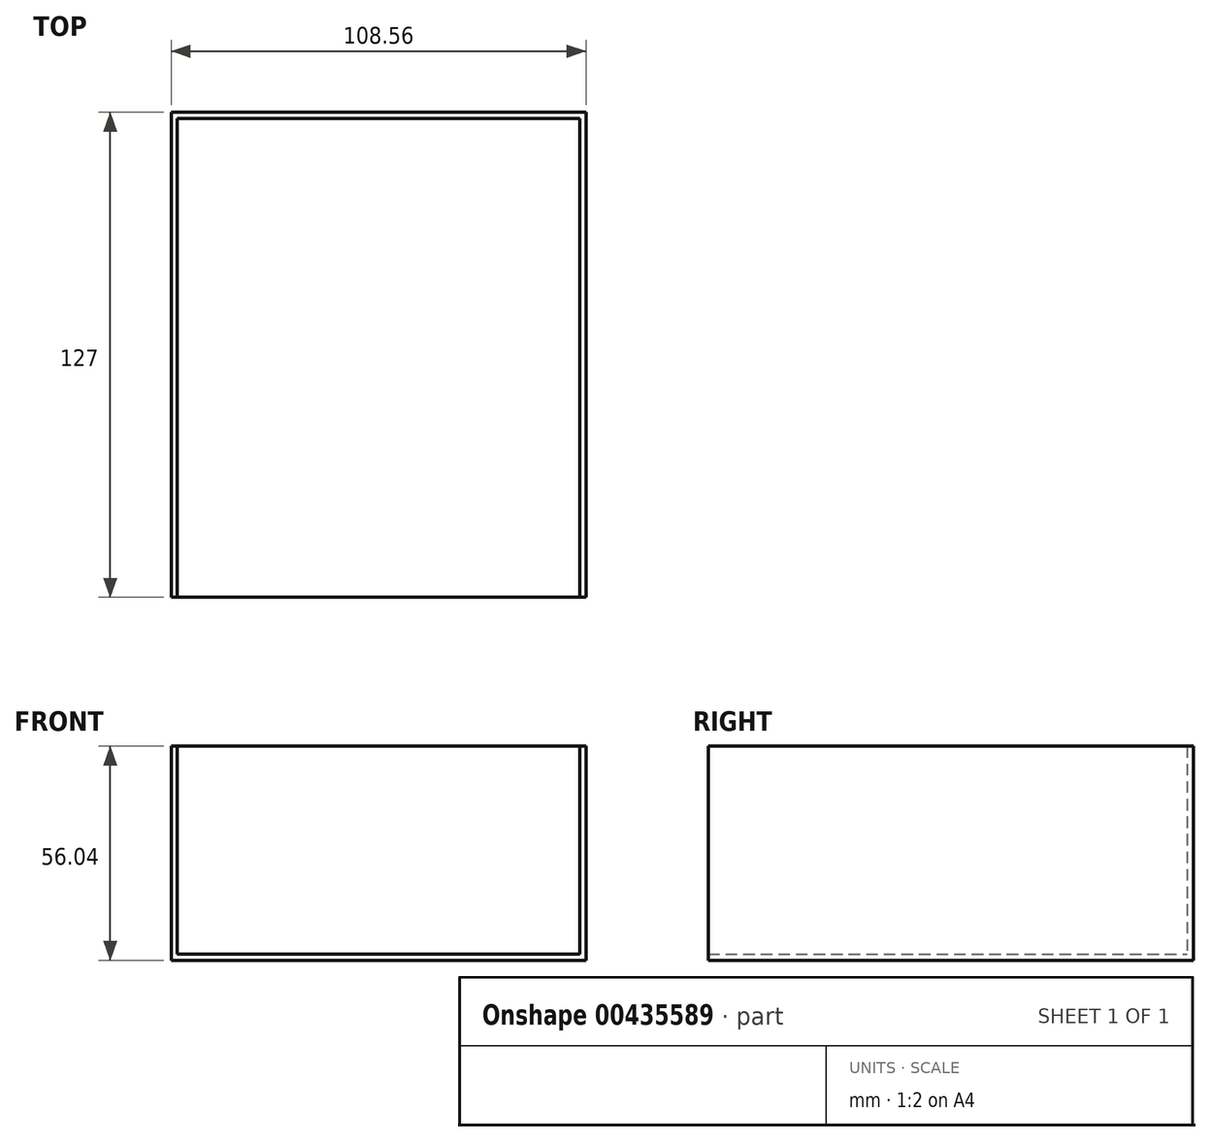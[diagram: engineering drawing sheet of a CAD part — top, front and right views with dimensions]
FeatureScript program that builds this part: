
annotation { "Feature Type Name" : "Feature", "Feature Type Description" : "" }
export const myFeature = defineFeature(function(context is Context, id is Id, definition is map)
    precondition{}
    {
        {
            var Q0;
            Q0=qCreatedBy(makeId("Front.planeOp"),FACE);
            var sketch = newSketch(context, id + "F0", { "sketchPlane" : qUnion([Q0])});
            skLineSegment(sketch, "E0.bottom", {"start": v(-54.28, 28.02) * mm, "end": v(54.28, 28.02) * mm});
            skLineSegment(sketch, "E0.top", {"start": v(-54.28, -28.02) * mm, "end": v(54.28, -28.02) * mm});
            skLineSegment(sketch, "E0.left", {"start": v(-54.28, 28.02) * mm, "end": v(-54.28, -28.02) * mm});
            skLineSegment(sketch, "E0.right", {"start": v(54.28, 28.02) * mm, "end": v(54.28, -28.02) * mm});
            skPoint(sketch, "E0.middle", {"position": v(0, 0) * mm});
            skSolve(sketch);
        }
        {
            var Q0;
            Q0 = qSketchRegion(id + "F0", true);
            extrude(context, id + "F1", {"entities" : qUnion([Q0]), "endBound" : BoundingType.SYMMETRIC, "depth" : 127 * mm});
        }
        {
            var Q0;
            Q0=makeQuery(id+"F1.opExtrude","SWEPT_FACE",FACE,{"disambiguationData":[OSD([sQuery(id+"F0.wireOp",EDGE,"E0.bottom")])]});
            var Q1;
            Q1=makeQuery(id+"F1.opExtrude","CAP_FACE",FACE,{"disambiguationData":[OSD([sQuery(id+"F0.wireOp",EDGE,"E0.bottom"),sQuery(id+"F0.wireOp",EDGE,"E0.top"),sQuery(id+"F0.wireOp",EDGE,"E0.left"),sQuery(id+"F0.wireOp",EDGE,"E0.right")])],"isStart":false});
            shell(context, id + "F2", {"entities" : qUnion([Q0, Q1]), "thickness" : 1.59 * mm});
        }
    });
